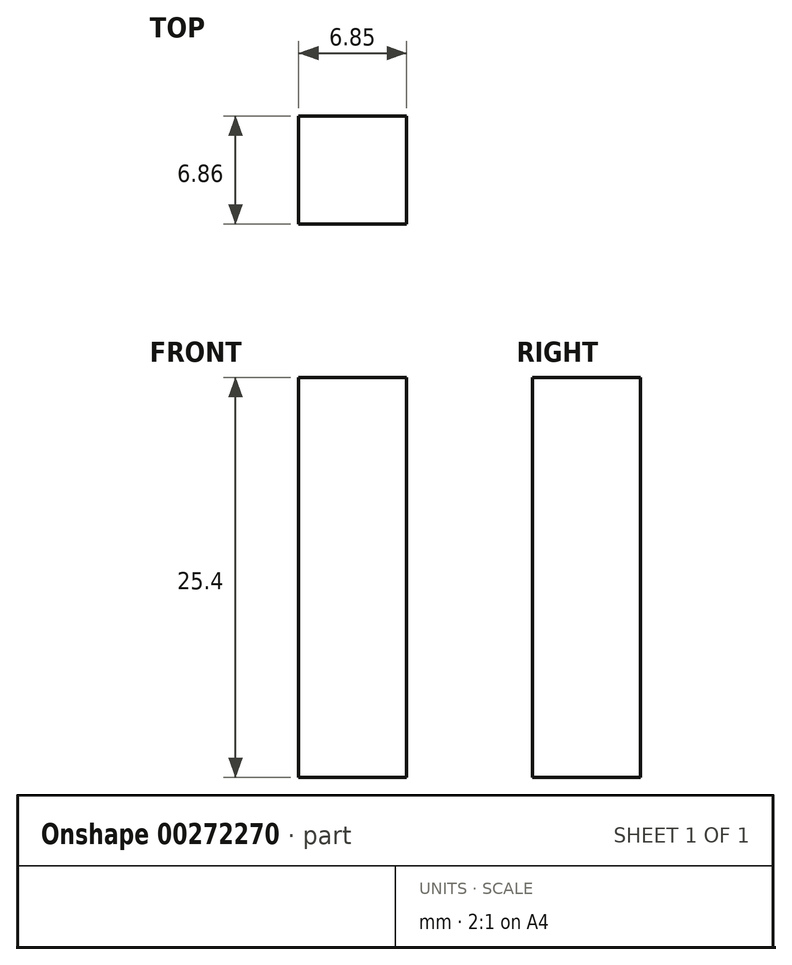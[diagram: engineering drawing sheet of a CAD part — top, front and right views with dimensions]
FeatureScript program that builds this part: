
annotation { "Feature Type Name" : "Feature", "Feature Type Description" : "" }
export const myFeature = defineFeature(function(context is Context, id is Id, definition is map)
    precondition{}
    {
        {
            var Q0;
            Q0=qCreatedBy(makeId("Top.planeOp"),FACE);
            var sketch = newSketch(context, id + "F0", { "sketchPlane" : qUnion([Q0])});
            skLineSegment(sketch, "E0.bottom", {"start": v(-39.7, 51.69) * mm, "end": v(-32.84, 51.69) * mm});
            skLineSegment(sketch, "E0.top", {"start": v(-39.7, 44.83) * mm, "end": v(-32.84, 44.83) * mm});
            skLineSegment(sketch, "E0.left", {"start": v(-39.7, 51.69) * mm, "end": v(-39.7, 44.83) * mm});
            skLineSegment(sketch, "E0.right", {"start": v(-32.84, 51.69) * mm, "end": v(-32.84, 44.83) * mm});
            skSolve(sketch);
        }
        {
            var Q0;
            Q0 = qSketchRegion(id + "F0", true);
            extrude(context, id + "F1", {"entities" : qUnion([Q0]), "depth" : 25.4 * mm});
        }
    });
